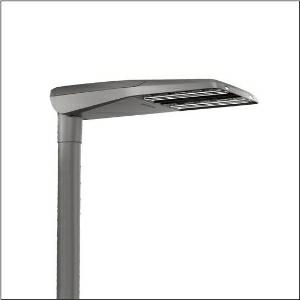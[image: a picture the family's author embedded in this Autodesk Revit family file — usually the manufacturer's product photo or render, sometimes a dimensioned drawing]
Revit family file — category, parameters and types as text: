
# Revit family: streetlight_sl_11_iq_midi___st1_2a_5xc3a41f08le_475e
name_source: partatom
category: Lighting Fixtures
units: mm (PartAtom-declared; Revit-internal decimal feet)

## family parameters
Cut with Voids When Loaded = No
Host = Face
Light Source = No
Part Type = Normal
Room Calculation Point = No
Round Connector Dimension = Use Diameter
Shared = No

## types (1)
- --- (1 x LED, 9590 lm, 60.4 W, 4000K)
    Apparent Load = 60 VA
    CIE Flux Codes = 32 70 96 100 100
    Color Rendering = 70
    Color Temperature = 4000K
    Default Elevation = 1800 mm
    Description = Streetlight SL 11 iQ midi, mast luminaire, primary light control with 3 zone facetted reflector, of plastic, silver coated, highly specular, primary optical cover: cover, of PMMA, transparent, light distribution: ST1.2a, light emission: direct distribution, primary light characteristic: asymmetric, installation type: post-top, side-entry, LED, High Power LED, rated luminous flux: 9.590lm, luminous efficacy: 159lm/W, light colour: 740, colour temperature: 4000K, control: Street-Remote, optimised constant luminous flux control (CLO 2.0), Desk-Remote (wireless, voltage-free reading and setting of iQ features in the workshop via application-optimized NFC function/RFID function), Light-Fading, Smart-Wire, Night-Set, Lumen-Switch, Temp-Guard, Auto-Match, with cable H07RN-F 5x 1.5mm², mains connection: 220..240V, AC, 50/60Hz, connection cable pre-assembled, cable length: 8,5m, start of lifetime: 60W, end of lifetime: 63W, reduction: 30W, luminaire housing, of diecast aluminium, powder-coated, Siteco® metallic grey (DB 702S), length: 780mm, width: 376mm, height: 118mm, spigot size: 60/76mm (post-top) and 42/60/76mm (side-entry), mast flange for spigot size: 42mm: 5XC10008XM4, 60mm: 5XC10008XM2, 76/60mm: 5XC10108XM1, equipment: standard, protection rating (complete): IP66, insulation class (complete): insulation class II (safety insulation), certification: CE, ENEC, VDE, impact resistance: IK09, permissible operating ambient temperature for outdoor applications: -25..+50°C, standard-compliant lighting for roads and squares, packaging unit: 1 piece

Light Distribution: ST1.2a
    Height = 118 mm
    Lamp = 1 x LED
    Lamp Light Flux = 9590 lm
    Lamp Power = 60.4 W
    Lamp count = 1
    Length = 780 mm
    Luminous efficacy = 159 lm/W
    Manufacturer = Siteco
    ModVariant = No
    Model = 5XC3A41F08LE
    Number of Poles = 1
    OnlyDefault = Yes
    Power Factor = 1
    Product Name = Streetlight SL 11 iQ midi | ST1.2a
    Product group = mast luminaire | pylon top
    ProductGroupID = 6100
    Protection Class = Protection class II
    Protection Degree = IP 66
    RLX_Detail_Level = 1
    RlxData = <blob elided: 70281 chars, md5=afa2dc6b>
    Socket = socket
    Standby Power = 0 W
    System Light Flux = 9590 lm
    System Power = 60 W
    Type Comments = factory setting: luminous flux: 100 % | dim-lin: 254 | 520 mA
    Type Image = l_1005960.jpg
    URL = http://relux.com
    VarID = @adj_120809
    Voltage = 0 V
    Weight = 0.00 kg
    Width = 376 mm

## geometry (parser evidence)
native form markers: Blend x4, Sweep x10
no freeform markers — native parametric forms only
